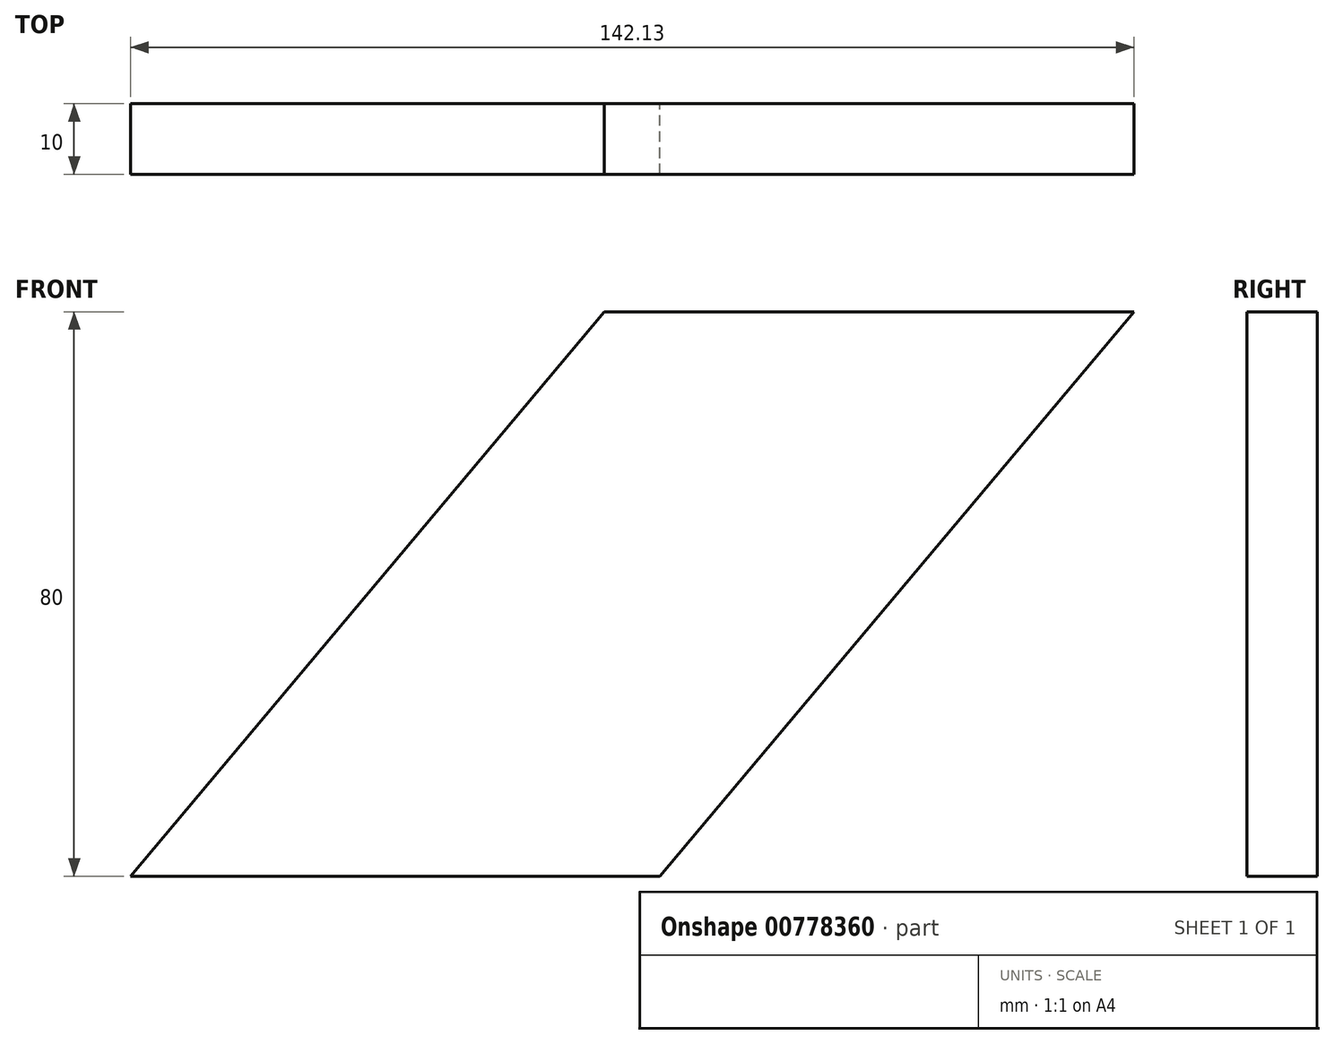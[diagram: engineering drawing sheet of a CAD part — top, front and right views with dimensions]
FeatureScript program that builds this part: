
annotation { "Feature Type Name" : "Feature", "Feature Type Description" : "" }
export const myFeature = defineFeature(function(context is Context, id is Id, definition is map)
    precondition{}
    {
        {
            var Q0;
            Q0=qCreatedBy(makeId("Front.planeOp"),FACE);
            var sketch = newSketch(context, id + "F0", { "sketchPlane" : qUnion([Q0])});
            skLineSegment(sketch, "E0", {"start": v(0, 0) * mm, "end": v(67.13, 80) * mm});
            skLineSegment(sketch, "E1", {"start": v(67.13, 80) * mm, "end": v(142.13, 80) * mm});
            skLineSegment(sketch, "E2", {"start": v(142.13, 80) * mm, "end": v(75, 0) * mm});
            skLineSegment(sketch, "E3", {"start": v(75, 0) * mm, "end": v(0, 0) * mm});
            skSolve(sketch);
        }
        {
            var Q0;
            Q0=makeQuery(id+"F0.imprint","IMPRINT",FACE,{"disambiguationData":[TD([[makeQuery(id+"F0.imprint","IMPRINT",EDGE,{"derivedFrom":sQuery(id+"F0.wireOp",EDGE,"E0")}),-1.0]])]});
            extrude(context, id + "F1", {"entities" : qUnion([Q0]), "depth" : 10 * mm, "offsetDistance" : 25 * mm});
        }
    });
